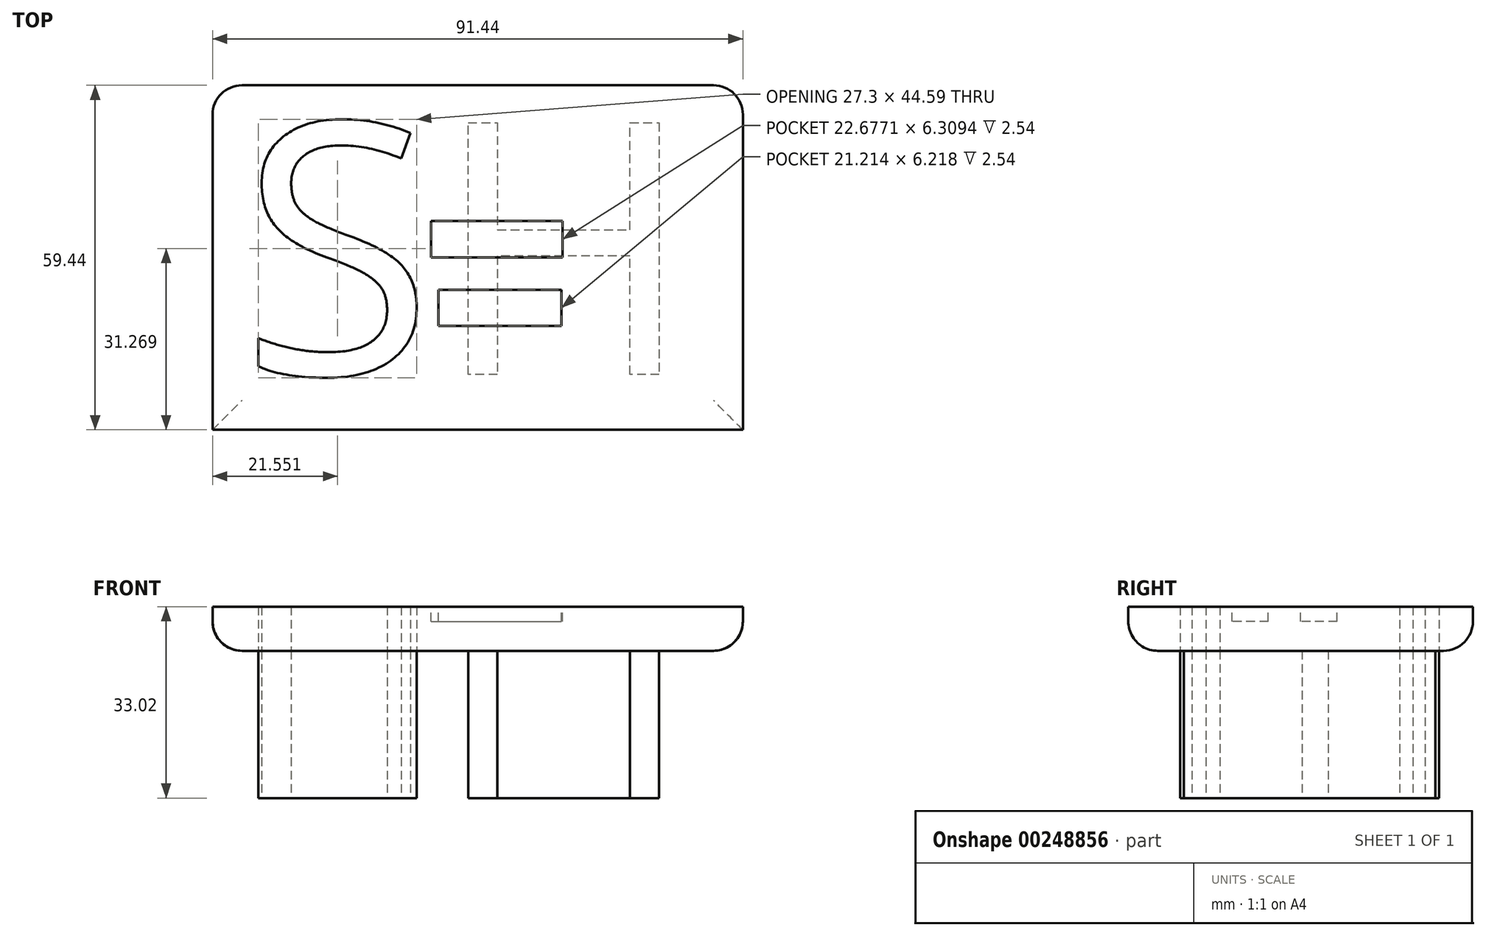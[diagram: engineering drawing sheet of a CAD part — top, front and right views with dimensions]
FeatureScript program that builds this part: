
annotation { "Feature Type Name" : "Feature", "Feature Type Description" : "" }
export const myFeature = defineFeature(function(context is Context, id is Id, definition is map)
    precondition{}
    {
        {
            var Q0;
            Q0=qCreatedBy(makeId("Top.planeOp"),FACE);
            var sketch = newSketch(context, id + "F0", { "sketchPlane" : qUnion([Q0])});
            skText(sketch, "E0", { "text": "SH", "fontName": "OpenSans-Regular.ttf"});
            const initialGuessF0  = {"E0": [-0.03017, -0.02015, 1, 0, 0.04375]};
            skSetInitialGuess(sketch, initialGuessF0);
            skSolve(sketch);
        }
        {
            var Q0;
            Q0=makeQuery(id+"F0.imprint","IMPRINT",FACE,{"disambiguationData":[TD([[makeQuery(id+"F0.imprint","IMPRINT",EDGE,{"derivedFrom":sQuery(id+"F0.wireOp",EDGE,"E0.sketch_text.stroke-0")}),-1.0]])]});
            var Q1;
            Q1 = qSketchRegion(id + "F0", true);
            extrude(context, id + "F1", {"entities" : qUnion([Q0, Q1]), "depth" : 25.4 * mm});
        }
        {
            var Q0;
            Q0=makeQuery(id+"F1.opExtrude","CAP_FACE",FACE,{"disambiguationData":[OSD([sQuery(id+"F0.wireOp",EDGE,"E0.sketch_text.stroke-0"),sQuery(id+"F0.wireOp",EDGE,"E0.sketch_text.stroke-1"),sQuery(id+"F0.wireOp",EDGE,"E0.sketch_text.stroke-2"),sQuery(id+"F0.wireOp",EDGE,"E0.sketch_text.stroke-3"),sQuery(id+"F0.wireOp",EDGE,"E0.sketch_text.stroke-4"),sQuery(id+"F0.wireOp",EDGE,"E0.sketch_text.stroke-5"),sQuery(id+"F0.wireOp",EDGE,"E0.sketch_text.stroke-6"),sQuery(id+"F0.wireOp",EDGE,"E0.sketch_text.stroke-7"),sQuery(id+"F0.wireOp",EDGE,"E0.sketch_text.stroke-8"),sQuery(id+"F0.wireOp",EDGE,"E0.sketch_text.stroke-9"),sQuery(id+"F0.wireOp",EDGE,"E0.sketch_text.stroke-10"),sQuery(id+"F0.wireOp",EDGE,"E0.sketch_text.stroke-11"),sQuery(id+"F0.wireOp",EDGE,"E0.sketch_text.stroke-12"),sQuery(id+"F0.wireOp",EDGE,"E0.sketch_text.stroke-13"),sQuery(id+"F0.wireOp",EDGE,"E0.sketch_text.stroke-14"),sQuery(id+"F0.wireOp",EDGE,"E0.sketch_text.stroke-15"),sQuery(id+"F0.wireOp",EDGE,"E0.sketch_text.stroke-16"),sQuery(id+"F0.wireOp",EDGE,"E0.sketch_text.stroke-17"),sQuery(id+"F0.wireOp",EDGE,"E0.sketch_text.stroke-18"),sQuery(id+"F0.wireOp",EDGE,"E0.sketch_text.stroke-19"),sQuery(id+"F0.wireOp",EDGE,"E0.sketch_text.stroke-20"),sQuery(id+"F0.wireOp",EDGE,"E0.sketch_text.stroke-21"),sQuery(id+"F0.wireOp",EDGE,"E0.sketch_text.stroke-22"),sQuery(id+"F0.wireOp",EDGE,"E0.sketch_text.stroke-23"),sQuery(id+"F0.wireOp",EDGE,"E0.sketch_text.stroke-24")])],"isStart":false});
            var sketch = newSketch(context, id + "F2", { "sketchPlane" : qUnion([Q0])});
            skLineSegment(sketch, "E1.bottom", {"start": v(-34.93, 29.72) * mm, "end": v(56.5, 29.72) * mm});
            skLineSegment(sketch, "E1.top", {"start": v(-34.93, -29.72) * mm, "end": v(56.5, -29.72) * mm});
            skLineSegment(sketch, "E1.left", {"start": v(-34.93, 29.72) * mm, "end": v(-34.93, -29.72) * mm});
            skLineSegment(sketch, "E1.right", {"start": v(56.5, 29.72) * mm, "end": v(56.5, -29.72) * mm});
            skSolve(sketch);
        }
        {
            var Q0;
            Q0=makeQuery(id+"F2.imprint","IMPRINT",FACE,{"disambiguationData":[TD([[makeQuery(id+"F2.imprint","IMPRINT",EDGE,{"derivedFrom":sQuery(id+"F2.wireOp",EDGE,"E1.bottom")}),-1.0]])]});
            extrude(context, id + "F3", {"entities" : qUnion([Q0]), "operationType" : NewBodyOperationType.ADD, "depth" : 7.62 * mm});
        }
        {
            var Q0;
            Q0=makeQuery(id+"F1.opExtrude","CAP_FACE",FACE,{"disambiguationData":[OSD([sQuery(id+"F0.wireOp",EDGE,"E0.sketch_text.stroke-0"),sQuery(id+"F0.wireOp",EDGE,"E0.sketch_text.stroke-1"),sQuery(id+"F0.wireOp",EDGE,"E0.sketch_text.stroke-2"),sQuery(id+"F0.wireOp",EDGE,"E0.sketch_text.stroke-3"),sQuery(id+"F0.wireOp",EDGE,"E0.sketch_text.stroke-4"),sQuery(id+"F0.wireOp",EDGE,"E0.sketch_text.stroke-5"),sQuery(id+"F0.wireOp",EDGE,"E0.sketch_text.stroke-6"),sQuery(id+"F0.wireOp",EDGE,"E0.sketch_text.stroke-7"),sQuery(id+"F0.wireOp",EDGE,"E0.sketch_text.stroke-8"),sQuery(id+"F0.wireOp",EDGE,"E0.sketch_text.stroke-9"),sQuery(id+"F0.wireOp",EDGE,"E0.sketch_text.stroke-10"),sQuery(id+"F0.wireOp",EDGE,"E0.sketch_text.stroke-11"),sQuery(id+"F0.wireOp",EDGE,"E0.sketch_text.stroke-12"),sQuery(id+"F0.wireOp",EDGE,"E0.sketch_text.stroke-13"),sQuery(id+"F0.wireOp",EDGE,"E0.sketch_text.stroke-14"),sQuery(id+"F0.wireOp",EDGE,"E0.sketch_text.stroke-15"),sQuery(id+"F0.wireOp",EDGE,"E0.sketch_text.stroke-16"),sQuery(id+"F0.wireOp",EDGE,"E0.sketch_text.stroke-17"),sQuery(id+"F0.wireOp",EDGE,"E0.sketch_text.stroke-18"),sQuery(id+"F0.wireOp",EDGE,"E0.sketch_text.stroke-19"),sQuery(id+"F0.wireOp",EDGE,"E0.sketch_text.stroke-20"),sQuery(id+"F0.wireOp",EDGE,"E0.sketch_text.stroke-21"),sQuery(id+"F0.wireOp",EDGE,"E0.sketch_text.stroke-22"),sQuery(id+"F0.wireOp",EDGE,"E0.sketch_text.stroke-23"),sQuery(id+"F0.wireOp",EDGE,"E0.sketch_text.stroke-24")])],"isStart":false});
            extrude(context, id + "F4", {"entities" : qUnion([Q0]), "depth" : 7.62 * mm});
        }
        {
            var Q0;
            Q0=makeQuery(id+"F3.opExtrude","CAP_EDGE",EDGE,{"disambiguationData":[OSD([sQuery(id+"F2.wireOp",EDGE,"E1.left")])],"isStart":true});
            var Q1;
            Q1=makeQuery(id+"F3.opExtrude","CAP_EDGE",EDGE,{"disambiguationData":[OSD([sQuery(id+"F2.wireOp",EDGE,"E1.top")])],"isStart":true});
            var Q2;
            Q2=makeQuery(id+"F3.opExtrude","CAP_EDGE",EDGE,{"disambiguationData":[OSD([sQuery(id+"F2.wireOp",EDGE,"E1.right")])],"isStart":true});
            fillet(context, id + "F5", {"entities" : qUnion([Q0, Q1, Q2]), "radius" : 5.08 * mm, "tangentPropagation" : true, "allowEdgeOverflow" : false});
        }
        {
            var Q0;
            Q0=makeQuery(id+"F3.opExtrude","CAP_FACE",FACE,{"disambiguationData":[OSD([sQuery(id+"F0.wireOp",EDGE,"E0.sketch_text.stroke-0"),sQuery(id+"F0.wireOp",EDGE,"E0.sketch_text.stroke-1"),sQuery(id+"F0.wireOp",EDGE,"E0.sketch_text.stroke-2"),sQuery(id+"F0.wireOp",EDGE,"E0.sketch_text.stroke-3"),sQuery(id+"F0.wireOp",EDGE,"E0.sketch_text.stroke-4"),sQuery(id+"F0.wireOp",EDGE,"E0.sketch_text.stroke-5"),sQuery(id+"F0.wireOp",EDGE,"E0.sketch_text.stroke-6"),sQuery(id+"F0.wireOp",EDGE,"E0.sketch_text.stroke-7"),sQuery(id+"F0.wireOp",EDGE,"E0.sketch_text.stroke-8"),sQuery(id+"F0.wireOp",EDGE,"E0.sketch_text.stroke-9"),sQuery(id+"F0.wireOp",EDGE,"E0.sketch_text.stroke-10"),sQuery(id+"F0.wireOp",EDGE,"E0.sketch_text.stroke-11"),sQuery(id+"F0.wireOp",EDGE,"E0.sketch_text.stroke-12"),sQuery(id+"F0.wireOp",EDGE,"E0.sketch_text.stroke-13"),sQuery(id+"F0.wireOp",EDGE,"E0.sketch_text.stroke-14"),sQuery(id+"F0.wireOp",EDGE,"E0.sketch_text.stroke-15"),sQuery(id+"F0.wireOp",EDGE,"E0.sketch_text.stroke-16"),sQuery(id+"F0.wireOp",EDGE,"E0.sketch_text.stroke-17"),sQuery(id+"F0.wireOp",EDGE,"E0.sketch_text.stroke-18"),sQuery(id+"F0.wireOp",EDGE,"E0.sketch_text.stroke-19"),sQuery(id+"F0.wireOp",EDGE,"E0.sketch_text.stroke-20"),sQuery(id+"F0.wireOp",EDGE,"E0.sketch_text.stroke-21"),sQuery(id+"F0.wireOp",EDGE,"E0.sketch_text.stroke-22"),sQuery(id+"F0.wireOp",EDGE,"E0.sketch_text.stroke-23"),sQuery(id+"F0.wireOp",EDGE,"E0.sketch_text.stroke-24"),sQuery(id+"F2.wireOp",EDGE,"E1.bottom"),sQuery(id+"F2.wireOp",EDGE,"E1.top"),sQuery(id+"F2.wireOp",EDGE,"E1.left"),sQuery(id+"F2.wireOp",EDGE,"E1.right")])],"isStart":false});
            var sketch = newSketch(context, id + "F6", { "sketchPlane" : qUnion([Q0])});
            skLineSegment(sketch, "E2.bottom", {"start": v(2.74, 6.3) * mm, "end": v(25.42, 6.3) * mm});
            skLineSegment(sketch, "E2.top", {"start": v(2.74, 0) * mm, "end": v(25.42, 0) * mm});
            skLineSegment(sketch, "E2.left", {"start": v(2.74, 6.3) * mm, "end": v(2.74, 0) * mm});
            skLineSegment(sketch, "E2.right", {"start": v(25.42, 6.3) * mm, "end": v(25.42, 0) * mm});
            skSolve(sketch);
        }
        {
            var Q0;
            Q0=makeQuery(id+"F6.imprint","IMPRINT",FACE,{"disambiguationData":[TD([[makeQuery(id+"F6.imprint","IMPRINT",EDGE,{"derivedFrom":sQuery(id+"F6.wireOp",EDGE,"E2.bottom")}),-1.0]])]});
            extrude(context, id + "F7", {"entities" : qUnion([Q0]), "operationType" : NewBodyOperationType.REMOVE, "oppositeDirection" : true, "depth" : 2.54 * mm});
        }
        {
            var Q0;
            Q0=makeQuery(id+"F3.opExtrude","CAP_EDGE",EDGE,{"disambiguationData":[OSD([sQuery(id+"F2.wireOp",EDGE,"E1.bottom")])],"isStart":true});
            fillet(context, id + "F8", {"entities" : qUnion([Q0]), "radius" : 5.08 * mm, "tangentPropagation" : true, "allowEdgeOverflow" : false});
        }
        {
            var Q0;
            Q0=makeQuery(id+"F3.opExtrude","CAP_FACE",FACE,{"disambiguationData":[OSD([sQuery(id+"F0.wireOp",EDGE,"E0.sketch_text.stroke-0"),sQuery(id+"F0.wireOp",EDGE,"E0.sketch_text.stroke-1"),sQuery(id+"F0.wireOp",EDGE,"E0.sketch_text.stroke-2"),sQuery(id+"F0.wireOp",EDGE,"E0.sketch_text.stroke-3"),sQuery(id+"F0.wireOp",EDGE,"E0.sketch_text.stroke-4"),sQuery(id+"F0.wireOp",EDGE,"E0.sketch_text.stroke-5"),sQuery(id+"F0.wireOp",EDGE,"E0.sketch_text.stroke-6"),sQuery(id+"F0.wireOp",EDGE,"E0.sketch_text.stroke-7"),sQuery(id+"F0.wireOp",EDGE,"E0.sketch_text.stroke-8"),sQuery(id+"F0.wireOp",EDGE,"E0.sketch_text.stroke-9"),sQuery(id+"F0.wireOp",EDGE,"E0.sketch_text.stroke-10"),sQuery(id+"F0.wireOp",EDGE,"E0.sketch_text.stroke-11"),sQuery(id+"F0.wireOp",EDGE,"E0.sketch_text.stroke-12"),sQuery(id+"F0.wireOp",EDGE,"E0.sketch_text.stroke-13"),sQuery(id+"F0.wireOp",EDGE,"E0.sketch_text.stroke-14"),sQuery(id+"F0.wireOp",EDGE,"E0.sketch_text.stroke-15"),sQuery(id+"F0.wireOp",EDGE,"E0.sketch_text.stroke-16"),sQuery(id+"F0.wireOp",EDGE,"E0.sketch_text.stroke-17"),sQuery(id+"F0.wireOp",EDGE,"E0.sketch_text.stroke-18"),sQuery(id+"F0.wireOp",EDGE,"E0.sketch_text.stroke-19"),sQuery(id+"F0.wireOp",EDGE,"E0.sketch_text.stroke-20"),sQuery(id+"F0.wireOp",EDGE,"E0.sketch_text.stroke-21"),sQuery(id+"F0.wireOp",EDGE,"E0.sketch_text.stroke-22"),sQuery(id+"F0.wireOp",EDGE,"E0.sketch_text.stroke-23"),sQuery(id+"F0.wireOp",EDGE,"E0.sketch_text.stroke-24"),sQuery(id+"F2.wireOp",EDGE,"E1.bottom"),sQuery(id+"F2.wireOp",EDGE,"E1.top"),sQuery(id+"F2.wireOp",EDGE,"E1.left"),sQuery(id+"F2.wireOp",EDGE,"E1.right")])],"isStart":false});
            var sketch = newSketch(context, id + "F9", { "sketchPlane" : qUnion([Q0])});
            skLineSegment(sketch, "E3.bottom", {"start": v(4.02, -5.58) * mm, "end": v(25.24, -5.58) * mm});
            skLineSegment(sketch, "E3.top", {"start": v(4.02, -11.8) * mm, "end": v(25.24, -11.8) * mm});
            skLineSegment(sketch, "E3.left", {"start": v(4.02, -5.58) * mm, "end": v(4.02, -11.8) * mm});
            skLineSegment(sketch, "E3.right", {"start": v(25.24, -5.58) * mm, "end": v(25.24, -11.8) * mm});
            skSolve(sketch);
        }
        {
            var Q0;
            Q0=makeQuery(id+"F9.imprint","IMPRINT",FACE,{"disambiguationData":[TD([[makeQuery(id+"F9.imprint","IMPRINT",EDGE,{"derivedFrom":sQuery(id+"F9.wireOp",EDGE,"E3.bottom")}),-1.0]])]});
            extrude(context, id + "F10", {"entities" : qUnion([Q0]), "operationType" : NewBodyOperationType.REMOVE, "oppositeDirection" : true, "depth" : 2.54 * mm});
        }
    });
